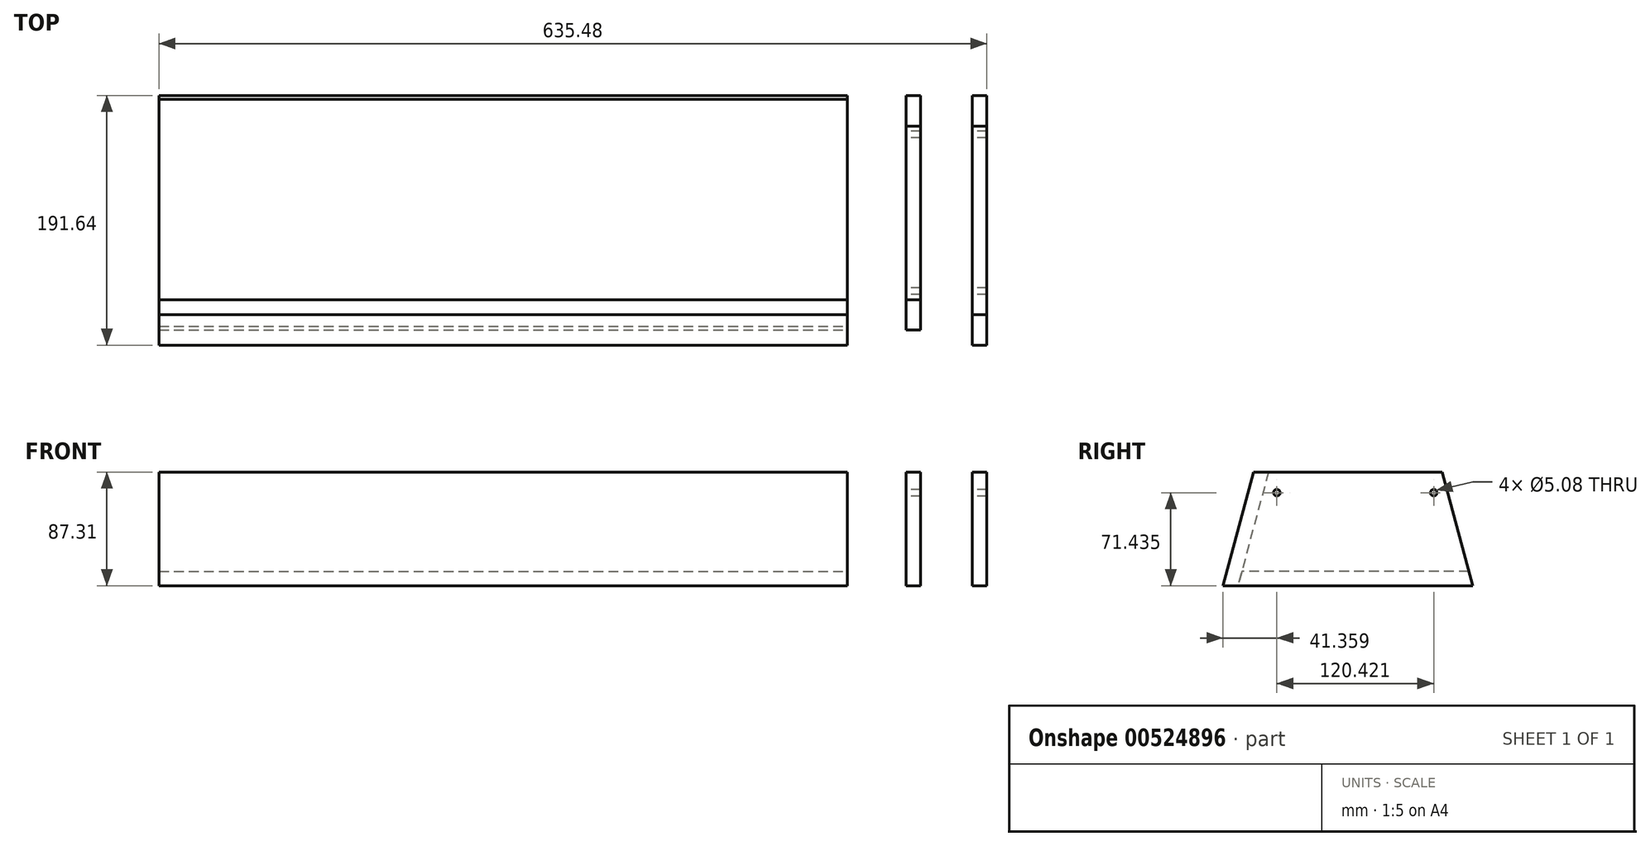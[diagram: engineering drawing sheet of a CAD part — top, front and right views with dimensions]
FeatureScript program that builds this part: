
annotation { "Feature Type Name" : "Feature", "Feature Type Description" : "" }
export const myFeature = defineFeature(function(context is Context, id is Id, definition is map)
    precondition{}
    {
        {
            var Q0;
            Q0=qCreatedBy(makeId("Right.planeOp"),FACE);
            var sketch = newSketch(context, id + "F0", { "sketchPlane" : qUnion([Q0])});
            skLineSegment(sketch, "E0", {"start": v(-66.68, 38.1) * mm, "end": v(66.68, 38.1) * mm});
            skLineSegment(sketch, "E1", {"start": v(66.68, 38.1) * mm, "end": v(87.1, -38.1) * mm});
            skLineSegment(sketch, "E2", {"start": v(87.1, -38.1) * mm, "end": v(-87.1, -38.1) * mm});
            skLineSegment(sketch, "E3", {"start": v(-87.1, -38.1) * mm, "end": v(-66.68, 38.1) * mm});
            skLineSegment(sketch, "E4", {"start": v(-66.68, 38.1) * mm, "end": v(-66.68, -38.1) * mm, "construction": true});
            skLineSegment(sketch, "E5", {"start": v(66.68, 38.1) * mm, "end": v(66.68, -38.1) * mm, "construction": true});
            skCircle(sketch, "E6", {"center": v(-60.21, 22.23) * mm, "radius": 2.54 * mm});
            skCircle(sketch, "E7", {"center": v(60.21, 22.23) * mm, "radius": 2.54 * mm});
            skLineSegment(sketch, "E8", {"start": v(0, 38.1) * mm, "end": v(0, -38.1) * mm, "construction": true});
            skLineSegment(sketch, "E9", {"start": v(-87.1, -38.1) * mm, "end": v(-90.07, -49.21) * mm});
            skLineSegment(sketch, "E10", {"start": v(-90.07, -49.21) * mm, "end": v(90.07, -49.21) * mm});
            skLineSegment(sketch, "E11", {"start": v(90.07, -49.21) * mm, "end": v(87.1, -38.1) * mm});
            skLineSegment(sketch, "E12", {"start": v(-66.68, 38.1) * mm, "end": v(-78.18, 38.1) * mm});
            skLineSegment(sketch, "E13", {"start": v(-78.18, 38.1) * mm, "end": v(-101.57, -49.21) * mm});
            skLineSegment(sketch, "E14", {"start": v(-101.57, -49.21) * mm, "end": v(-90.07, -49.21) * mm});
            skSolve(sketch);
        }
        {
            var Q0;
            Q0=makeQuery(id+"F0.imprint","IMPRINT",FACE,{"disambiguationData":[TD([[makeQuery(id+"F0.imprint","IMPRINT",EDGE,{"derivedFrom":sQuery(id+"F0.wireOp",EDGE,"E0")}),-1.0]])]});
            var Q1;
            Q1=makeQuery(id+"F0.imprint","IMPRINT",FACE,{"disambiguationData":[TD([[makeQuery(id+"F0.imprint","IMPRINT",EDGE,{"derivedFrom":sQuery(id+"F0.wireOp",EDGE,"E2")}),1.0]])]});
            extrude(context, id + "F1", {"entities" : qUnion([Q0, Q1]), "endBound" : BoundingType.SYMMETRIC, "depth" : 11.1 * mm, "offsetDistance" : 25.4 * mm});
        }
        {
            var Q0;
            Q0 = qSketchRegion(id + "F0", true);
            extrude(context, id + "F2", {"entities" : qUnion([Q0]), "endBound" : BoundingType.SYMMETRIC, "depth" : 11.1 * mm, "offsetDistance" : 25.4 * mm});
        }
        {
            var Q0;
            Q0=makeQuery(id+"F2.opExtrude","SWEPT_BODY",BODY,{"disambiguationData":[OSD([sQuery(id+"F0.wireOp",EDGE,"E0"),sQuery(id+"F0.wireOp",EDGE,"E1"),sQuery(id+"F0.wireOp",EDGE,"E6"),sQuery(id+"F0.wireOp",EDGE,"E7"),sQuery(id+"F0.wireOp",EDGE,"E10"),sQuery(id+"F0.wireOp",EDGE,"E11"),sQuery(id+"F0.wireOp",EDGE,"E12"),sQuery(id+"F0.wireOp",EDGE,"E13"),sQuery(id+"F0.wireOp",EDGE,"E14")])]});
            var Q1;
            Q1=makeQuery(id+"F2.opExtrude","SWEPT_EDGE",EDGE,{"disambiguationData":[OSD([sQuery(id+"F0.wireOp",EDGE,"E12"),sQuery(id+"F0.wireOp",EDGE,"E13")])]});
            var Q2;
            Q2=makeQuery(id+"F2.opExtrude","SWEPT_EDGE",EDGE,{"disambiguationData":[OSD([sQuery(id+"F0.wireOp",EDGE,"E12"),sQuery(id+"F0.wireOp",EDGE,"E13")])]});
            transform(context, id + "F3", {"entities" : qUnion([Q0]), "transformType" : TransformType.TRANSLATION_DISTANCE, "transformDirection" : qUnion([Q2]), "distance" : 50.8 * mm, "oppositeDirection" : true, "makeCopy" : false});
        }
        {
            var Q0;
            Q0=makeQuery(id+"F0.imprint","IMPRINT",FACE,{"disambiguationData":[TD([[makeQuery(id+"F0.imprint","IMPRINT",EDGE,{"derivedFrom":sQuery(id+"F0.wireOp",EDGE,"E2")}),1.0]])]});
            extrude(context, id + "F4", {"entities" : qUnion([Q0]), "oppositeDirection" : true, "depth" : 528.32 * mm, "offsetDistance" : 25.4 * mm});
        }
        {
            var Q0;
            Q0=makeQuery(id+"F4.opExtrude","SWEPT_BODY",BODY,{"disambiguationData":[OSD([sQuery(id+"F0.wireOp",EDGE,"E2"),sQuery(id+"F0.wireOp",EDGE,"E9"),sQuery(id+"F0.wireOp",EDGE,"E10"),sQuery(id+"F0.wireOp",EDGE,"E11")])]});
            var Q1;
            Q1=makeQuery(id+"F4.opExtrude","SWEPT_EDGE",EDGE,{"disambiguationData":[OSD([sQuery(id+"F0.wireOp",EDGE,"E2"),sQuery(id+"F0.wireOp",EDGE,"E3"),sQuery(id+"F0.wireOp",EDGE,"E9")])]});
            transform(context, id + "F5", {"entities" : qUnion([Q0]), "transformType" : TransformType.TRANSLATION_DISTANCE, "transformDirection" : qUnion([Q1]), "distance" : 50.8 * mm, "oppositeDirection" : true, "makeCopy" : false});
        }
        {
            var Q0;
            Q0=makeQuery(id+"F0.imprint","IMPRINT",FACE,{"disambiguationData":[TD([[makeQuery(id+"F0.imprint","IMPRINT",EDGE,{"derivedFrom":sQuery(id+"F0.wireOp",EDGE,"E3")}),1.0]])]});
            extrude(context, id + "F6", {"entities" : qUnion([Q0]), "oppositeDirection" : true, "depth" : 528.32 * mm, "offsetDistance" : 25.4 * mm});
        }
        {
            var Q0;
            Q0=makeQuery(id+"F6.opExtrude","SWEPT_BODY",BODY,{"disambiguationData":[OSD([sQuery(id+"F0.wireOp",EDGE,"E3"),sQuery(id+"F0.wireOp",EDGE,"E9"),sQuery(id+"F0.wireOp",EDGE,"E12"),sQuery(id+"F0.wireOp",EDGE,"E13"),sQuery(id+"F0.wireOp",EDGE,"E14")])]});
            var Q1;
            Q1=makeQuery(id+"F6.opExtrude","SWEPT_EDGE",EDGE,{"disambiguationData":[OSD([sQuery(id+"F0.wireOp",EDGE,"E12"),sQuery(id+"F0.wireOp",EDGE,"E13")])]});
            transform(context, id + "F7", {"entities" : qUnion([Q0]), "transformType" : TransformType.TRANSLATION_DISTANCE, "transformDirection" : qUnion([Q1]), "distance" : 50.8 * mm, "oppositeDirection" : true, "makeCopy" : false});
        }
    });
